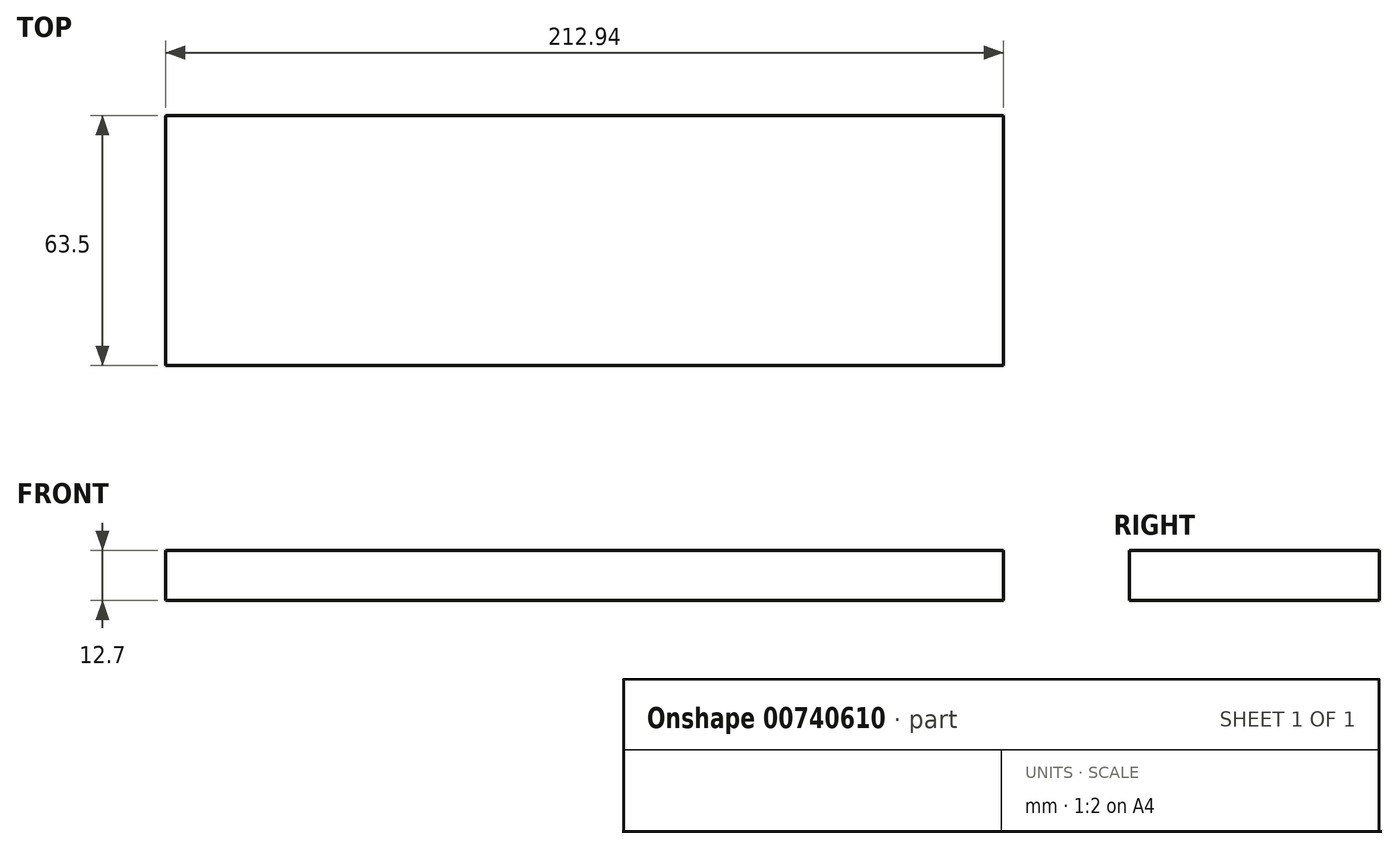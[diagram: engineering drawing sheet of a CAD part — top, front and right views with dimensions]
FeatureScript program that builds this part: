
annotation { "Feature Type Name" : "Feature", "Feature Type Description" : "" }
export const myFeature = defineFeature(function(context is Context, id is Id, definition is map)
    precondition{}
    {
        {
            var Q0;
            Q0=qCreatedBy(makeId("Top.planeOp"),FACE);
            var sketch = newSketch(context, id + "F0", { "sketchPlane" : qUnion([Q0])});
            skLineSegment(sketch, "E0.bottom", {"start": v(106.47, -31.75) * mm, "end": v(-106.47, -31.75) * mm});
            skLineSegment(sketch, "E0.top", {"start": v(106.47, 31.75) * mm, "end": v(-106.47, 31.75) * mm});
            skLineSegment(sketch, "E0.left", {"start": v(106.47, -31.75) * mm, "end": v(106.47, 31.75) * mm});
            skLineSegment(sketch, "E0.right", {"start": v(-106.47, -31.75) * mm, "end": v(-106.47, 31.75) * mm});
            skPoint(sketch, "E0.middle", {"position": v(0, 0) * mm});
            skSolve(sketch);
        }
        {
            var Q0;
            Q0=makeQuery(id+"F0.imprint","IMPRINT",FACE,{"disambiguationData":[TD([[makeQuery(id+"F0.imprint","IMPRINT",EDGE,{"derivedFrom":sQuery(id+"F0.wireOp",EDGE,"E0.bottom")}),-1.0]])]});
            extrude(context, id + "F1", {"entities" : qUnion([Q0]), "oppositeDirection" : true, "depth" : 12.7 * mm, "offsetDistance" : 25.4 * mm});
        }
    });
